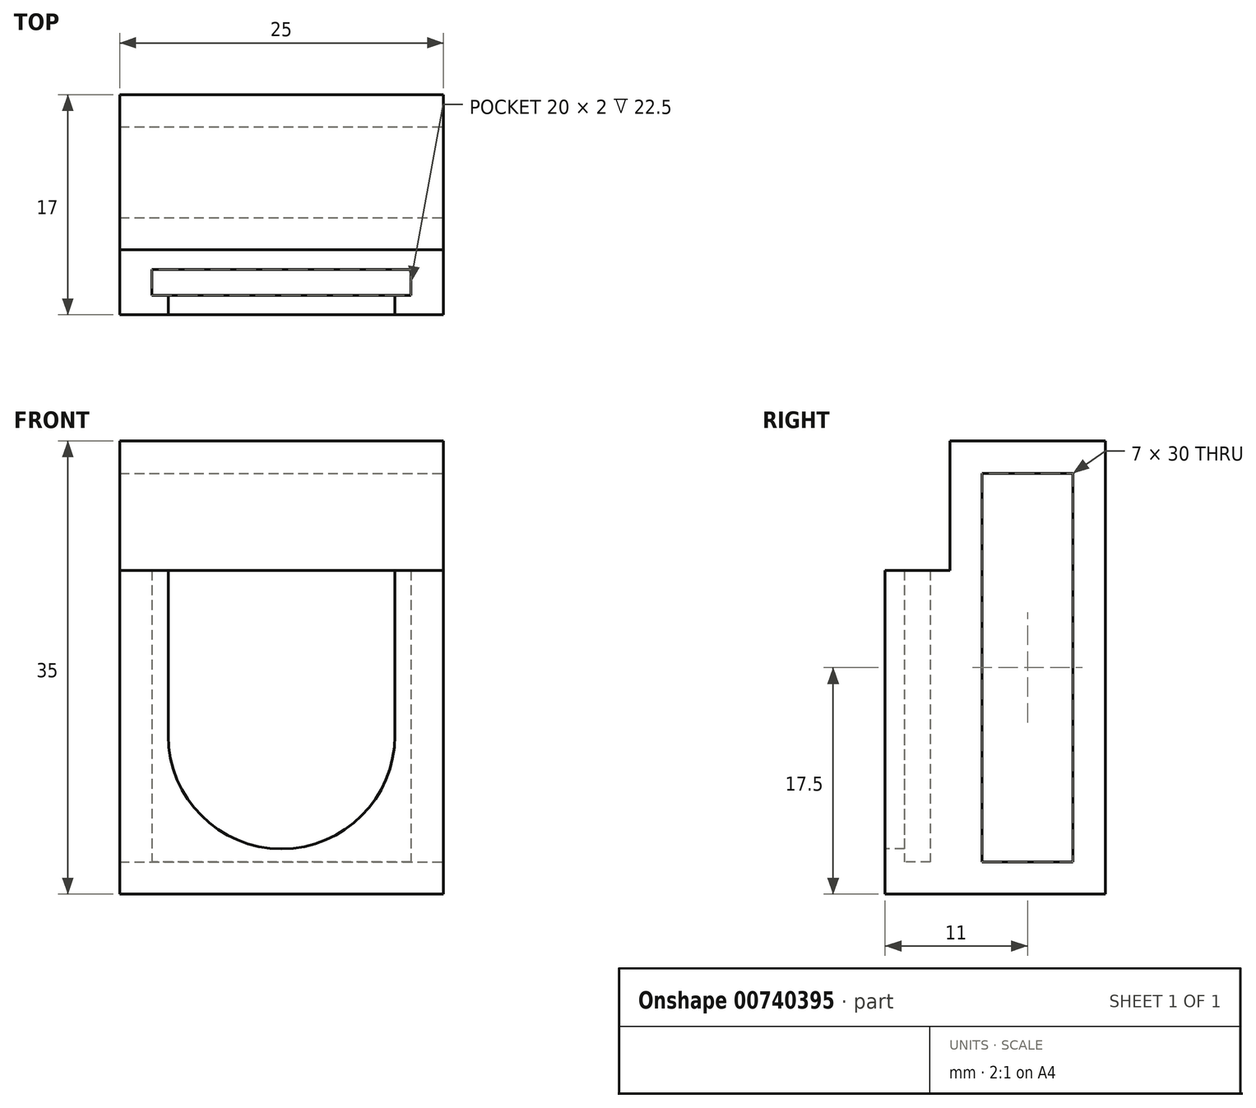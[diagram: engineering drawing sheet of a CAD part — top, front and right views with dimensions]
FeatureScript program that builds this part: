
annotation { "Feature Type Name" : "Feature", "Feature Type Description" : "" }
export const myFeature = defineFeature(function(context is Context, id is Id, definition is map)
    precondition{}
    {
        {
            var Q0;
            Q0=qCreatedBy(makeId("Top.planeOp"),FACE);
            var sketch = newSketch(context, id + "F0", { "sketchPlane" : qUnion([Q0])});
            skLineSegment(sketch, "E0.bottom", {"start": v(10, 1) * mm, "end": v(-10, 1) * mm});
            skLineSegment(sketch, "E0.top", {"start": v(10, -1) * mm, "end": v(-10, -1) * mm});
            skLineSegment(sketch, "E0.left", {"start": v(10, 1) * mm, "end": v(10, -1) * mm});
            skLineSegment(sketch, "E0.right", {"start": v(-10, 1) * mm, "end": v(-10, -1) * mm});
            skPoint(sketch, "E0.middle", {"position": v(0, 0) * mm});
            skLineSegment(sketch, "E1.bottom", {"start": v(12.5, 2.5) * mm, "end": v(-12.5, 2.5) * mm});
            skLineSegment(sketch, "E1.top", {"start": v(12.5, -2.5) * mm, "end": v(-12.5, -2.5) * mm});
            skLineSegment(sketch, "E1.left", {"start": v(12.5, 2.5) * mm, "end": v(12.5, -2.5) * mm});
            skLineSegment(sketch, "E1.right", {"start": v(-12.5, 2.5) * mm, "end": v(-12.5, -2.5) * mm});
            skLineSegment(sketch, "E2.top", {"start": v(12.5, 14.5) * mm, "end": v(-12.5, 14.5) * mm});
            skLineSegment(sketch, "E2.left", {"start": v(12.5, 2.5) * mm, "end": v(12.5, 14.5) * mm});
            skLineSegment(sketch, "E2.right", {"start": v(-12.5, 2.5) * mm, "end": v(-12.5, 14.5) * mm});
            skLineSegment(sketch, "E3.bottom", {"start": v(-10, 12) * mm, "end": v(10, 12) * mm});
            skLineSegment(sketch, "E3.top", {"start": v(-10, 5) * mm, "end": v(10, 5) * mm});
            skLineSegment(sketch, "E3.left", {"start": v(-10, 12) * mm, "end": v(-10, 5) * mm});
            skLineSegment(sketch, "E3.right", {"start": v(10, 12) * mm, "end": v(10, 5) * mm});
            skLineSegment(sketch, "E4", {"start": v(-10, 12) * mm, "end": v(-12.5, 12) * mm});
            skLineSegment(sketch, "E5", {"start": v(-10, 5) * mm, "end": v(-12.5, 5) * mm});
            skLineSegment(sketch, "E6", {"start": v(10, 12) * mm, "end": v(12.5, 12) * mm});
            skLineSegment(sketch, "E7", {"start": v(10, 5) * mm, "end": v(12.5, 5) * mm});
            skSolve(sketch);
        }
        {
            var Q0;
            Q0=makeQuery(id+"F0.imprint","IMPRINT",FACE,{"disambiguationData":[TD([[makeQuery(id+"F0.imprint","IMPRINT",EDGE,{"derivedFrom":sQuery(id+"F0.wireOp",EDGE,"E0.bottom")}),1.0]])]});
            extrude(context, id + "F1", {"entities" : qUnion([Q0]), "depth" : 2.5 * mm, "offsetDistance" : 25 * mm});
        }
        {
            var Q0;
            Q0=makeQuery(id+"F0.imprint","IMPRINT",FACE,{"disambiguationData":[TD([[makeQuery(id+"F0.imprint","IMPRINT",EDGE,{"derivedFrom":sQuery(id+"F0.wireOp",EDGE,"E0.bottom")}),-1.0]])]});
            extrude(context, id + "F2", {"entities" : qUnion([Q0]), "operationType" : NewBodyOperationType.ADD, "depth" : 25 * mm, "offsetDistance" : 25 * mm});
        }
        {
            var Q0;
            Q0=makeQuery(id+"F2.opExtrude","SWEPT_FACE",FACE,{"disambiguationData":[OSD([sQuery(id+"F0.wireOp",EDGE,"E1.top")])]});
            var sketch = newSketch(context, id + "F3", { "sketchPlane" : qUnion([Q0])});
            skCircle(sketch, "E8", {"center": v(0, 12.25) * mm, "radius": 8.75 * mm});
            skLineSegment(sketch, "E9", {"start": v(-8.75, 25) * mm, "end": v(-8.75, 12.25) * mm});
            skLineSegment(sketch, "E10", {"start": v(8.75, 25) * mm, "end": v(8.75, 12.25) * mm});
            skSolve(sketch);
        }
        {
            var Q0;
            Q0 = qSketchRegion(id + "F3", true);
            var Q1;
            {var subQ0=sQuery(id+"F3.wireOp",EDGE,"E9");Q1=makeQuery(id+"F3.imprint","IMPRINT",FACE,{"disambiguationData":[TD([[makeQuery(id+"F3.imprint","IMPRINT",EDGE,{"derivedFrom":subQ0}),1.0]])]});}
            extrude(context, id + "F4", {"entities" : qUnion([Q0, Q1]), "operationType" : NewBodyOperationType.REMOVE, "oppositeDirection" : true, "depth" : 2.5 * mm, "offsetDistance" : 25 * mm});
        }
        {
            var Q0;
            {var subQ1=sQuery(id+"F0.wireOp",EDGE,"E2.top");Q0=makeQuery(id+"F0.imprint","IMPRINT",FACE,{"disambiguationData":[TD([[makeQuery(id+"F0.imprint","IMPRINT",EDGE,{"derivedFrom":subQ1}),1.0]])]});}
            var Q1;
            Q1=makeQuery(id+"F0.imprint","IMPRINT",FACE,{"disambiguationData":[TD([[makeQuery(id+"F0.imprint","IMPRINT",EDGE,{"derivedFrom":sQuery(id+"F0.wireOp",EDGE,"E3.left")}),-1.0]])]});
            var Q2;
            Q2=makeQuery(id+"F0.imprint","IMPRINT",FACE,{"disambiguationData":[TD([[makeQuery(id+"F0.imprint","IMPRINT",EDGE,{"derivedFrom":sQuery(id+"F0.wireOp",EDGE,"E3.bottom")}),-1.0]])]});
            var Q3;
            {var subQ1=sQuery(id+"F0.wireOp",EDGE,"E1.bottom");Q3=makeQuery(id+"F0.imprint","IMPRINT",FACE,{"disambiguationData":[TD([[makeQuery(id+"F0.imprint","IMPRINT",EDGE,{"derivedFrom":subQ1}),-1.0]])]});}
            var Q4;
            Q4=makeQuery(id+"F0.imprint","IMPRINT",FACE,{"disambiguationData":[TD([[makeQuery(id+"F0.imprint","IMPRINT",EDGE,{"derivedFrom":sQuery(id+"F0.wireOp",EDGE,"E3.right")}),1.0]])]});
            extrude(context, id + "F5", {"entities" : qUnion([Q0, Q1, Q2, Q3, Q4]), "operationType" : NewBodyOperationType.ADD, "depth" : 35 * mm, "offsetDistance" : 25 * mm});
        }
        {
            var Q0;
            Q0=makeQuery(id+"F0.imprint","IMPRINT",FACE,{"disambiguationData":[TD([[makeQuery(id+"F0.imprint","IMPRINT",EDGE,{"derivedFrom":sQuery(id+"F0.wireOp",EDGE,"E3.right")}),1.0]])]});
            var Q1;
            Q1=makeQuery(id+"F0.imprint","IMPRINT",FACE,{"disambiguationData":[TD([[makeQuery(id+"F0.imprint","IMPRINT",EDGE,{"derivedFrom":sQuery(id+"F0.wireOp",EDGE,"E3.bottom")}),-1.0]])]});
            var Q2;
            Q2=makeQuery(id+"F0.imprint","IMPRINT",FACE,{"disambiguationData":[TD([[makeQuery(id+"F0.imprint","IMPRINT",EDGE,{"derivedFrom":sQuery(id+"F0.wireOp",EDGE,"E3.left")}),-1.0]])]});
            extrude(context, id + "F6", {"entities" : qUnion([Q0, Q1, Q2]), "operationType" : NewBodyOperationType.REMOVE, "depth" : 32.5 * mm, "offsetDistance" : 25 * mm});
        }
        {
            var Q0;
            Q0=makeQuery(id+"F0.imprint","IMPRINT",FACE,{"disambiguationData":[TD([[makeQuery(id+"F0.imprint","IMPRINT",EDGE,{"derivedFrom":sQuery(id+"F0.wireOp",EDGE,"E3.right")}),1.0]])]});
            var Q1;
            Q1=makeQuery(id+"F0.imprint","IMPRINT",FACE,{"disambiguationData":[TD([[makeQuery(id+"F0.imprint","IMPRINT",EDGE,{"derivedFrom":sQuery(id+"F0.wireOp",EDGE,"E3.bottom")}),-1.0]])]});
            var Q2;
            Q2=makeQuery(id+"F0.imprint","IMPRINT",FACE,{"disambiguationData":[TD([[makeQuery(id+"F0.imprint","IMPRINT",EDGE,{"derivedFrom":sQuery(id+"F0.wireOp",EDGE,"E3.left")}),-1.0]])]});
            var Q3;
            {var subQ1=sQuery(id+"F0.wireOp",EDGE,"E2.top");Q3=makeQuery(id+"F0.imprint","IMPRINT",FACE,{"disambiguationData":[TD([[makeQuery(id+"F0.imprint","IMPRINT",EDGE,{"derivedFrom":subQ1}),1.0]])]});}
            var Q4;
            {var subQ1=sQuery(id+"F0.wireOp",EDGE,"E1.bottom");Q4=makeQuery(id+"F0.imprint","IMPRINT",FACE,{"disambiguationData":[TD([[makeQuery(id+"F0.imprint","IMPRINT",EDGE,{"derivedFrom":subQ1}),-1.0]])]});}
            extrude(context, id + "F7", {"entities" : qUnion([Q0, Q1, Q2, Q3, Q4]), "operationType" : NewBodyOperationType.ADD, "depth" : 2.5 * mm, "offsetDistance" : 25 * mm});
        }
    });
